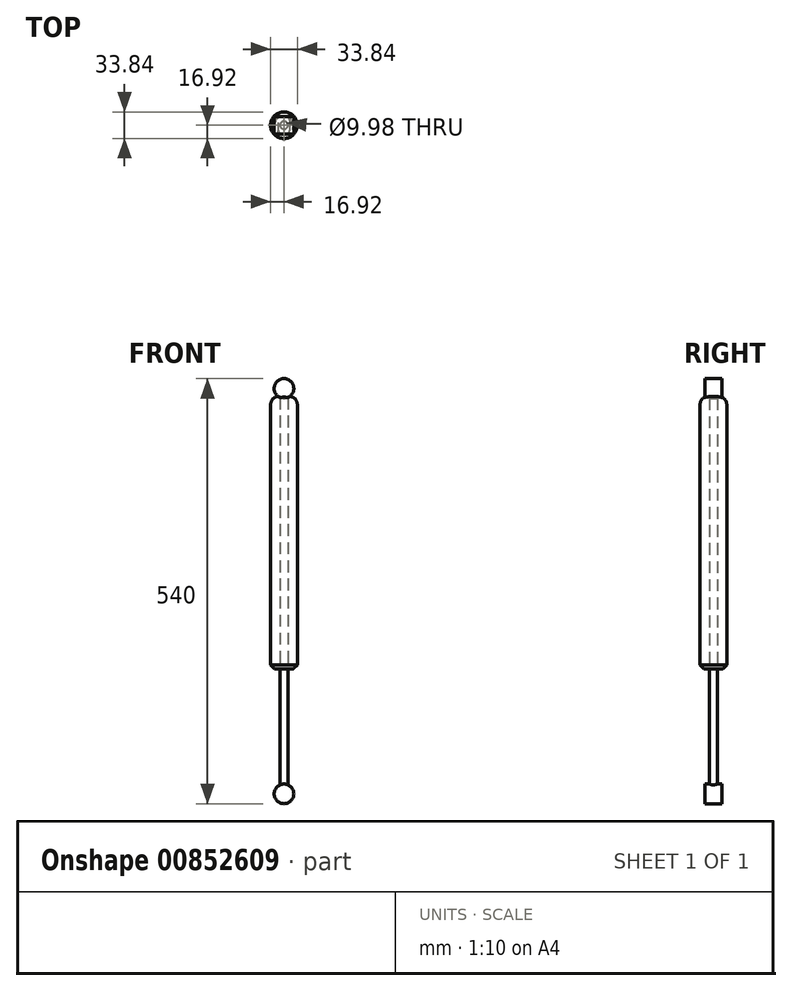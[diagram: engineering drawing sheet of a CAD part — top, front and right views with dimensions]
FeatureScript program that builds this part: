
annotation { "Feature Type Name" : "Feature", "Feature Type Description" : "" }
export const myFeature = defineFeature(function(context is Context, id is Id, definition is map)
    precondition{}
    {
        {
            var Q0;
            Q0=qCreatedBy(makeId("Top.planeOp"),FACE);
            var sketch = newSketch(context, id + "F0", { "sketchPlane" : qUnion([Q0])});
            skCircle(sketch, "E0", {"center": v(0, 0) * mm, "radius": 4.99 * mm});
            skSolve(sketch);
        }
        {
            var Q0;
            Q0=makeQuery(id+"F0.imprint","IMPRINT",FACE,{"disambiguationData":[TD([[makeQuery(id+"F0.imprint","IMPRINT",EDGE,{"derivedFrom":sQuery(id+"F0.wireOp",EDGE,"E0")}),1.0]])]});
            extrude(context, id + "F1", {"entities" : qUnion([Q0]), "depth" : 152 * mm, "offsetDistance" : 25 * mm});
        }
        {
            var Q0;
            Q0=qCreatedBy(makeId("Front.planeOp"),FACE);
            var sketch = newSketch(context, id + "F2", { "sketchPlane" : qUnion([Q0])});
            skCircle(sketch, "E1", {"center": v(0, -6.63) * mm, "radius": 12.5 * mm});
            skCircle(sketch, "E2", {"center": v(0, 508.37) * mm, "radius": 12.5 * mm});
            skSolve(sketch);
        }
        {
            var Q0;
            Q0=makeQuery(id+"F1.opExtrude","CAP_FACE",FACE,{"disambiguationData":[OSD([sQuery(id+"F0.wireOp",EDGE,"E0")])],"isStart":false});
            var sketch = newSketch(context, id + "F3", { "sketchPlane" : qUnion([Q0])});
            skCircle(sketch, "E3", {"center": v(0, 0) * mm, "radius": 16.92 * mm});
            skSolve(sketch);
        }
        {
            var Q0;
            Q0=makeQuery(id+"F3.imprint","IMPRINT",FACE,{"disambiguationData":[TD([[makeQuery(id+"F3.imprint","IMPRINT",EDGE,{"derivedFrom":sQuery(id+"F3.wireOp",EDGE,"E3")}),1.0]])]});
            extrude(context, id + "F4", {"entities" : qUnion([Q0]), "depth" : 346.2 * mm, "offsetDistance" : 25 * mm});
        }
        {
            var Q0;
            Q0=makeQuery(id+"F4.opExtrude","CAP_EDGE",EDGE,{"disambiguationData":[OSD([sQuery(id+"F3.wireOp",EDGE,"E3")])],"isStart":false});
            fillet(context, id + "F5", {"entities" : qUnion([Q0]), "radius" : 10.14 * mm, "tangentPropagation" : true, "allowEdgeOverflow" : false});
        }
        {
            var Q0;
            Q0=makeQuery(id+"F4.opExtrude","CAP_EDGE",EDGE,{"disambiguationData":[OSD([sQuery(id+"F3.wireOp",EDGE,"E3")])],"isStart":true});
            chamfer(context, id + "F6", {"entities" : qUnion([Q0]), "width" : 5 * mm, "tangentPropagation" : true});
        }
        {
            var Q0;
            Q0=makeQuery(id+"F2.imprint","IMPRINT",FACE,{"disambiguationData":[TD([[makeQuery(id+"F2.imprint","IMPRINT",EDGE,{"derivedFrom":sQuery(id+"F2.wireOp",EDGE,"E1")}),1.0]])]});
            var Q1;
            Q1=makeQuery(id+"F2.imprint","IMPRINT",FACE,{"disambiguationData":[TD([[makeQuery(id+"F2.imprint","IMPRINT",EDGE,{"derivedFrom":sQuery(id+"F2.wireOp",EDGE,"E2")}),1.0]])]});
            extrude(context, id + "F7", {"entities" : qUnion([Q0, Q1]), "operationType" : NewBodyOperationType.ADD, "depth" : 22 * mm, "offsetDistance" : 25 * mm, "symmetric" : true});
        }
    });
